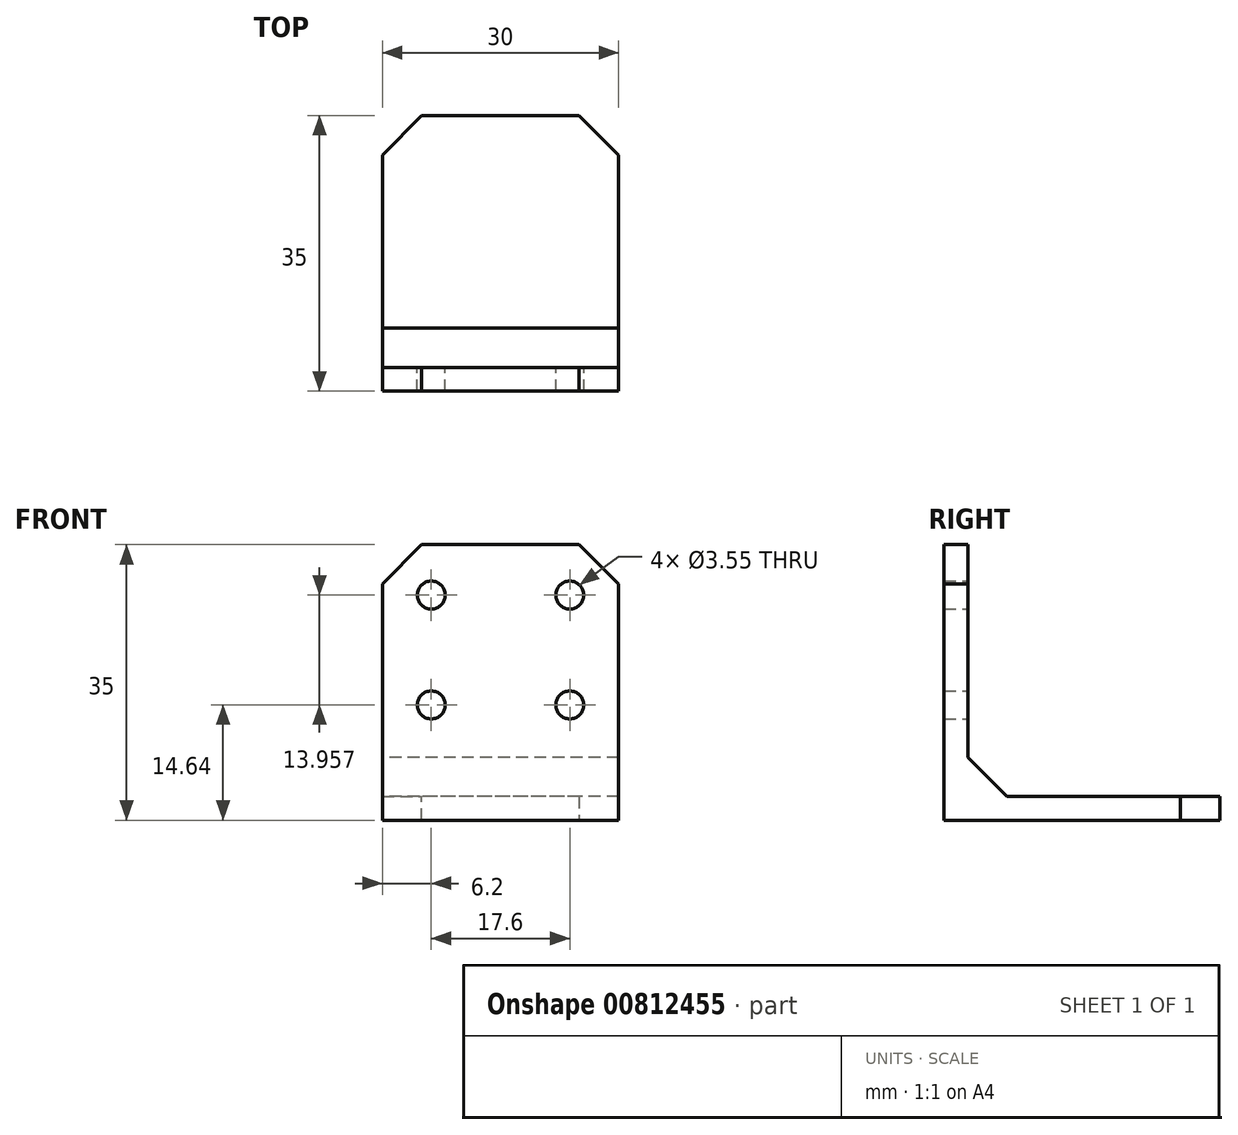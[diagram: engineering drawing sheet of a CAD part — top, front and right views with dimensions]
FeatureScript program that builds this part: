
annotation { "Feature Type Name" : "Feature", "Feature Type Description" : "" }
export const myFeature = defineFeature(function(context is Context, id is Id, definition is map)
    precondition{}
    {
        {
            var Q0;
            Q0=qCreatedBy(makeId("Right.planeOp"),FACE);
            var sketch = newSketch(context, id + "F0", { "sketchPlane" : qUnion([Q0])});
            skLineSegment(sketch, "E0", {"start": v(-26.83, 11.56) * mm, "end": v(-26.83, -23.44) * mm});
            skLineSegment(sketch, "E1", {"start": v(-26.83, -23.44) * mm, "end": v(8.17, -23.44) * mm});
            skLineSegment(sketch, "E2", {"start": v(8.17, -23.44) * mm, "end": v(8.17, -20.44) * mm});
            skLineSegment(sketch, "E3", {"start": v(8.17, -20.44) * mm, "end": v(-23.83, -20.44) * mm});
            skLineSegment(sketch, "E4", {"start": v(-23.83, -20.44) * mm, "end": v(-23.83, 11.56) * mm});
            skLineSegment(sketch, "E5", {"start": v(-23.83, 11.56) * mm, "end": v(-26.83, 11.56) * mm});
            skSolve(sketch);
        }
        {
            var Q0;
            Q0 = qSketchRegion(id + "F0", true);
            extrude(context, id + "F1", {"entities" : qUnion([Q0]), "depth" : 15 * mm, "offsetDistance" : 25 * mm, "hasSecondDirection" : true, "secondDirectionOppositeDirection" : true, "secondDirectionDepth" : 15 * mm});
        }
        {
            var Q0;
            Q0=makeQuery(id+"F1.opExtrude","SWEPT_FACE",FACE,{"disambiguationData":[OSD([sQuery(id+"F0.wireOp",EDGE,"E4")])]});
            var sketch = newSketch(context, id + "F2", { "sketchPlane" : qUnion([Q0])});
            skCircle(sketch, "E6", {"center": v(-8.8, 5.16) * mm, "radius": 1.77 * mm});
            skCircle(sketch, "E7", {"center": v(8.8, 5.16) * mm, "radius": 1.77 * mm});
            skCircle(sketch, "E8", {"center": v(8.8, -8.8) * mm, "radius": 1.77 * mm});
            skCircle(sketch, "E9", {"center": v(-8.8, -8.8) * mm, "radius": 1.77 * mm});
            skSolve(sketch);
        }
        {
            var Q0;
            Q0 = qSketchRegion(id + "F2", true);
            extrude(context, id + "F3", {"entities" : qUnion([Q0]), "operationType" : NewBodyOperationType.REMOVE, "oppositeDirection" : true, "depth" : 25 * mm, "offsetDistance" : 25 * mm});
        }
        {
            var Q0;
            Q0=qCreatedBy(makeId("Right.planeOp"),FACE);
            var sketch = newSketch(context, id + "F4", { "sketchPlane" : qUnion([Q0])});
            skLineSegment(sketch, "E10.bottom", {"start": v(-18.83, -15.44) * mm, "end": v(-23.83, -15.44) * mm});
            skLineSegment(sketch, "E10.top", {"start": v(-18.83, -20.44) * mm, "end": v(-23.83, -20.44) * mm});
            skLineSegment(sketch, "E10.left", {"start": v(-18.83, -15.44) * mm, "end": v(-18.83, -20.44) * mm});
            skLineSegment(sketch, "E10.right", {"start": v(-23.83, -15.44) * mm, "end": v(-23.83, -20.44) * mm});
            skSolve(sketch);
        }
        {
            var Q0;
            Q0 = qSketchRegion(id + "F4", true);
            extrude(context, id + "F5", {"entities" : qUnion([Q0]), "operationType" : NewBodyOperationType.ADD, "depth" : 15 * mm, "offsetDistance" : 25 * mm, "hasSecondDirection" : true, "secondDirectionOppositeDirection" : true, "secondDirectionDepth" : 15 * mm});
        }
        {
            var Q0;
            Q0=makeQuery(id+"F5.opExtrude","SWEPT_EDGE",EDGE,{"disambiguationData":[OSD([sQuery(id+"F4.wireOp",EDGE,"E10.bottom"),sQuery(id+"F4.wireOp",EDGE,"E10.left")])]});
            chamfer(context, id + "F6", {"entities" : qUnion([Q0]), "width" : 5 * mm, "tangentPropagation" : true});
        }
        {
            var Q0;
            Q0=makeQuery(id+"F1.opExtrude","CAP_EDGE",EDGE,{"disambiguationData":[OSD([sQuery(id+"F0.wireOp",EDGE,"E5")])],"isStart":true});
            chamfer(context, id + "F7", {"entities" : qUnion([Q0]), "width" : 5 * mm, "tangentPropagation" : true});
        }
        {
            var Q0;
            Q0=makeQuery(id+"F1.opExtrude","CAP_EDGE",EDGE,{"disambiguationData":[OSD([sQuery(id+"F0.wireOp",EDGE,"E5")])],"isStart":false});
            chamfer(context, id + "F8", {"entities" : qUnion([Q0]), "width" : 5 * mm, "tangentPropagation" : true});
        }
        {
            var Q0;
            Q0=makeQuery(id+"F1.opExtrude","CAP_EDGE",EDGE,{"disambiguationData":[OSD([sQuery(id+"F0.wireOp",EDGE,"E2")])],"isStart":false});
            chamfer(context, id + "F9", {"entities" : qUnion([Q0]), "width" : 5 * mm, "tangentPropagation" : true});
        }
        {
            var Q0;
            Q0=makeQuery(id+"F1.opExtrude","CAP_EDGE",EDGE,{"disambiguationData":[OSD([sQuery(id+"F0.wireOp",EDGE,"E2")])],"isStart":true});
            chamfer(context, id + "F10", {"entities" : qUnion([Q0]), "width" : 5 * mm, "tangentPropagation" : true});
        }
    });
